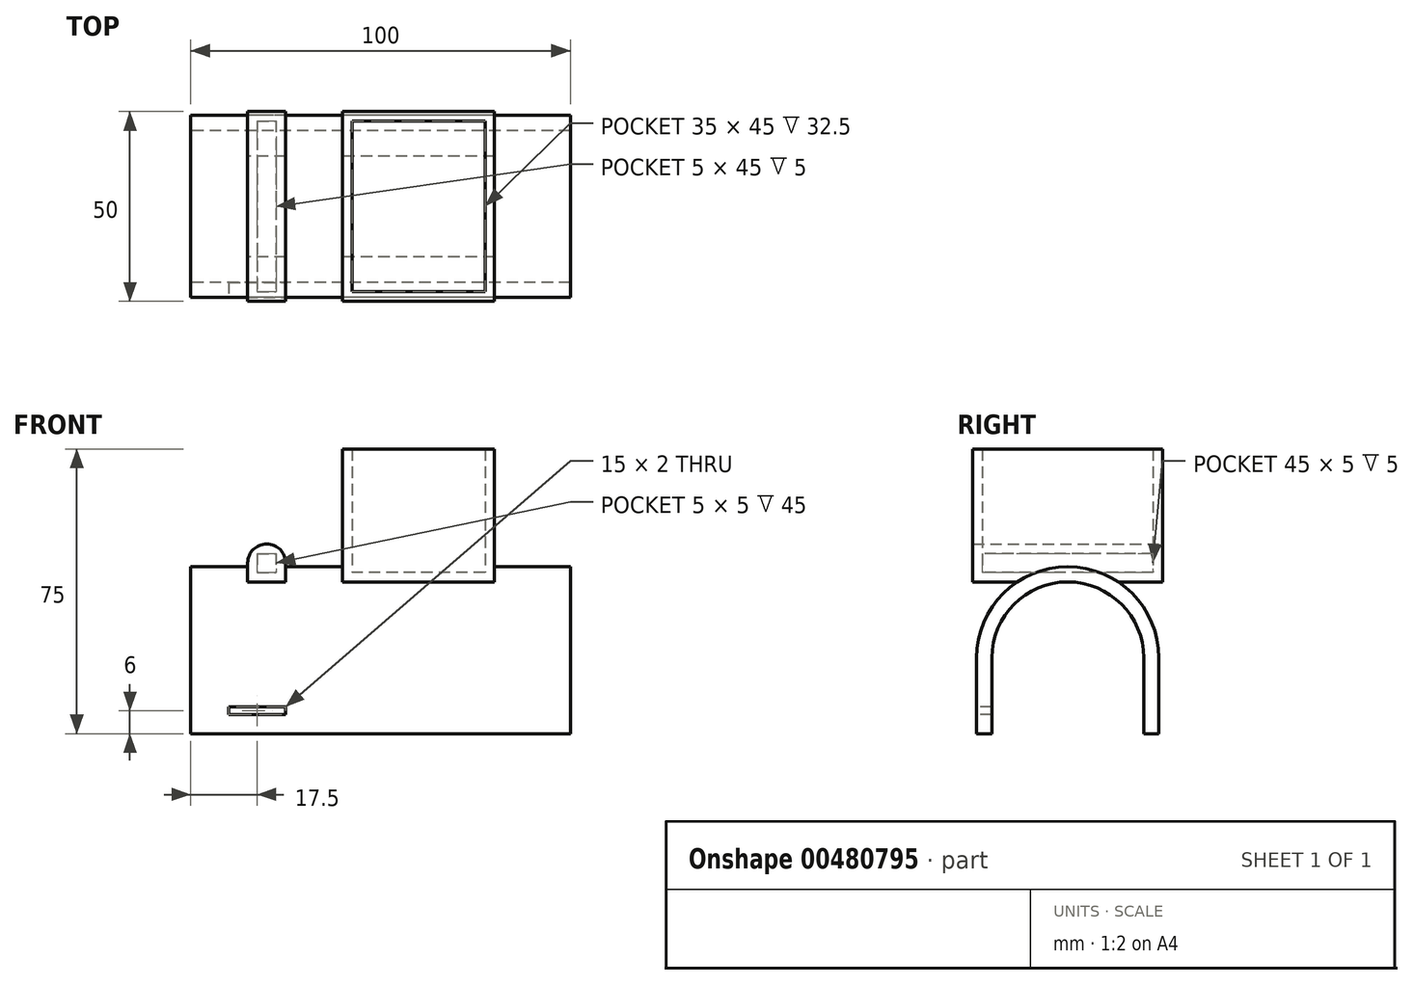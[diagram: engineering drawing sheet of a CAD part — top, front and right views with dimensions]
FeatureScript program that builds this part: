
annotation { "Feature Type Name" : "Feature", "Feature Type Description" : "" }
export const myFeature = defineFeature(function(context is Context, id is Id, definition is map)
    precondition{}
    {
        {
            var Q0;
            Q0=qCreatedBy(makeId("Right.planeOp"),FACE);
            var sketch = newSketch(context, id + "F0", { "sketchPlane" : qUnion([Q0])});
            skLineSegment(sketch, "E0.bottom", {"start": v(-20, 0) * mm, "end": v(-24, 0) * mm});
            skLineSegment(sketch, "E0.top", {"start": v(-20, 20) * mm, "end": v(-24, 20) * mm});
            skLineSegment(sketch, "E0.left", {"start": v(-20, 0) * mm, "end": v(-20, 20) * mm});
            skLineSegment(sketch, "E0.right", {"start": v(-24, 0) * mm, "end": v(-24, 20) * mm});
            skLineSegment(sketch, "E1.MirrorCS", {"start": v(20, 0) * mm, "end": v(24, 0) * mm});
            skLineSegment(sketch, "E2.MirrorCS", {"start": v(20, 20) * mm, "end": v(24, 20) * mm});
            skLineSegment(sketch, "E3.MirrorCS", {"start": v(24, 0) * mm, "end": v(24, 20) * mm});
            skLineSegment(sketch, "E4.MirrorCS", {"start": v(20, 0) * mm, "end": v(20, 20) * mm});
            skArc(sketch, "E5", {"start": v(20, 20) * mm, "mid": v(0, 40) * mm, "end": v(-20, 20) * mm});
            skArc(sketch, "E6", {"start": v(24, 20) * mm, "mid": v(0, 44) * mm, "end": v(-24, 20) * mm});
            skSolve(sketch);
        }
        {
            var Q0;
            Q0=qCreatedBy(makeId("Top.planeOp"),FACE);
            cPlane(context, id + "F1", {"entities" : qUnion([Q0]), "cplaneType" : CPlaneType.OFFSET, "offset" : 40 * mm, "width" : 150 * mm, "height" : 150 * mm});
        }
        {
            var Q0;
            Q0=qSketchRegion(id+"F0",true);
            extrude(context, id + "F2", {"entities" : qUnion([Q0]), "depth" : 100 * mm});
        }
        {
            var Q0;
            Q0=qCreatedBy(id+"F1.planeOp",FACE);
            var sketch = newSketch(context, id + "F3", { "sketchPlane" : qUnion([Q0])});
            skLineSegment(sketch, "E7.bottom", {"start": v(15, 25) * mm, "end": v(25, 25) * mm});
            skLineSegment(sketch, "E7.top", {"start": v(15, -25) * mm, "end": v(25, -25) * mm});
            skLineSegment(sketch, "E7.left", {"start": v(15, 25) * mm, "end": v(15, -25) * mm});
            skLineSegment(sketch, "E7.right", {"start": v(25, 25) * mm, "end": v(25, -25) * mm});
            skLineSegment(sketch, "E8.bottom", {"start": v(80, 25) * mm, "end": v(40, 25) * mm});
            skLineSegment(sketch, "E8.top", {"start": v(80, -25) * mm, "end": v(40, -25) * mm});
            skLineSegment(sketch, "E8.left", {"start": v(80, 25) * mm, "end": v(80, -25) * mm});
            skLineSegment(sketch, "E8.right", {"start": v(40, 25) * mm, "end": v(40, -25) * mm});
            skSolve(sketch);
        }
        {
            var Q0;
            Q0=qSketchRegion(id+"F3",true);
            extrude(context, id + "F4", {"entities" : qUnion([Q0]), "operationType" : NewBodyOperationType.ADD, "depth" : 10 * mm});
        }
        {
            var Q0;
            Q0=makeQuery(id+"F4.opExtrude","CAP_FACE",FACE,{"disambiguationData":[OSD([sQuery(id+"F3.wireOp",EDGE,"E8.bottom"),sQuery(id+"F3.wireOp",EDGE,"E8.top"),sQuery(id+"F3.wireOp",EDGE,"E8.left"),sQuery(id+"F3.wireOp",EDGE,"E8.right")])],"isStart":false});
            extrude(context, id + "F5", {"entities" : qUnion([Q0]), "operationType" : NewBodyOperationType.ADD, "depth" : 25 * mm});
        }
        {
            var Q0;
            Q0=makeQuery(id+"F5.opExtrude","CAP_FACE",FACE,{"disambiguationData":[OSD([sQuery(id+"F3.wireOp",EDGE,"E8.bottom"),sQuery(id+"F3.wireOp",EDGE,"E8.top"),sQuery(id+"F3.wireOp",EDGE,"E8.left"),sQuery(id+"F3.wireOp",EDGE,"E8.right")])],"isStart":false});
            shell(context, id + "F6", {"entities" : qUnion([Q0]), "thickness" : 2.5 * mm});
        }
        {
            var Q0;
            Q0=makeQuery(id+"F4.opExtrude","CAP_EDGE",EDGE,{"disambiguationData":[OSD([sQuery(id+"F3.wireOp",EDGE,"E7.left")])],"isStart":false});
            fillet(context, id + "F7", {"entities" : qUnion([Q0]), "radius" : 5 * mm, "tangentPropagation" : true, "allowEdgeOverflow" : false});
        }
        {
            var Q0;
            Q0=makeQuery(id+"F4.opExtrude","CAP_EDGE",EDGE,{"disambiguationData":[OSD([sQuery(id+"F3.wireOp",EDGE,"E7.right")])],"isStart":false});
            fillet(context, id + "F8", {"entities" : qUnion([Q0]), "radius" : 5 * mm, "tangentPropagation" : true, "allowEdgeOverflow" : false});
        }
        {
            var Q0;
            Q0=makeQuery(id+"F2.opExtrude","SWEPT_FACE",FACE,{"disambiguationData":[OSD([sQuery(id+"F0.wireOp",EDGE,"E0.right")])]});
            cPlane(context, id + "F9", {"entities" : qUnion([Q0]), "cplaneType" : CPlaneType.OFFSET, "offset" : 0 * mm, "width" : 150 * mm, "height" : 150 * mm});
        }
        {
            var Q0;
            Q0=makeQuery(id+"F2.opExtrude","SWEPT_FACE",FACE,{"disambiguationData":[OSD([sQuery(id+"F0.wireOp",EDGE,"E0.right")])]});
            var sketch = newSketch(context, id + "F10", { "sketchPlane" : qUnion([Q0])});
            skLineSegment(sketch, "E9.bottom", {"start": v(10, 7) * mm, "end": v(25, 7) * mm});
            skLineSegment(sketch, "E9.top", {"start": v(10, 5) * mm, "end": v(25, 5) * mm});
            skLineSegment(sketch, "E9.left", {"start": v(10, 7) * mm, "end": v(10, 5) * mm});
            skLineSegment(sketch, "E9.right", {"start": v(25, 7) * mm, "end": v(25, 5) * mm});
            skSolve(sketch);
        }
        {
            var Q0;
            Q0=makeQuery(id+"F10.imprint","IMPRINT",FACE,{"disambiguationData":[TD([[makeQuery(id+"F10.imprint","IMPRINT",EDGE,{"derivedFrom":sQuery(id+"F10.wireOp",EDGE,"E9.bottom")}),-1.0]])]});
            extrude(context, id + "F11", {"entities" : qUnion([Q0]), "operationType" : NewBodyOperationType.REMOVE, "oppositeDirection" : true, "depth" : 25 * mm});
        }
    });
